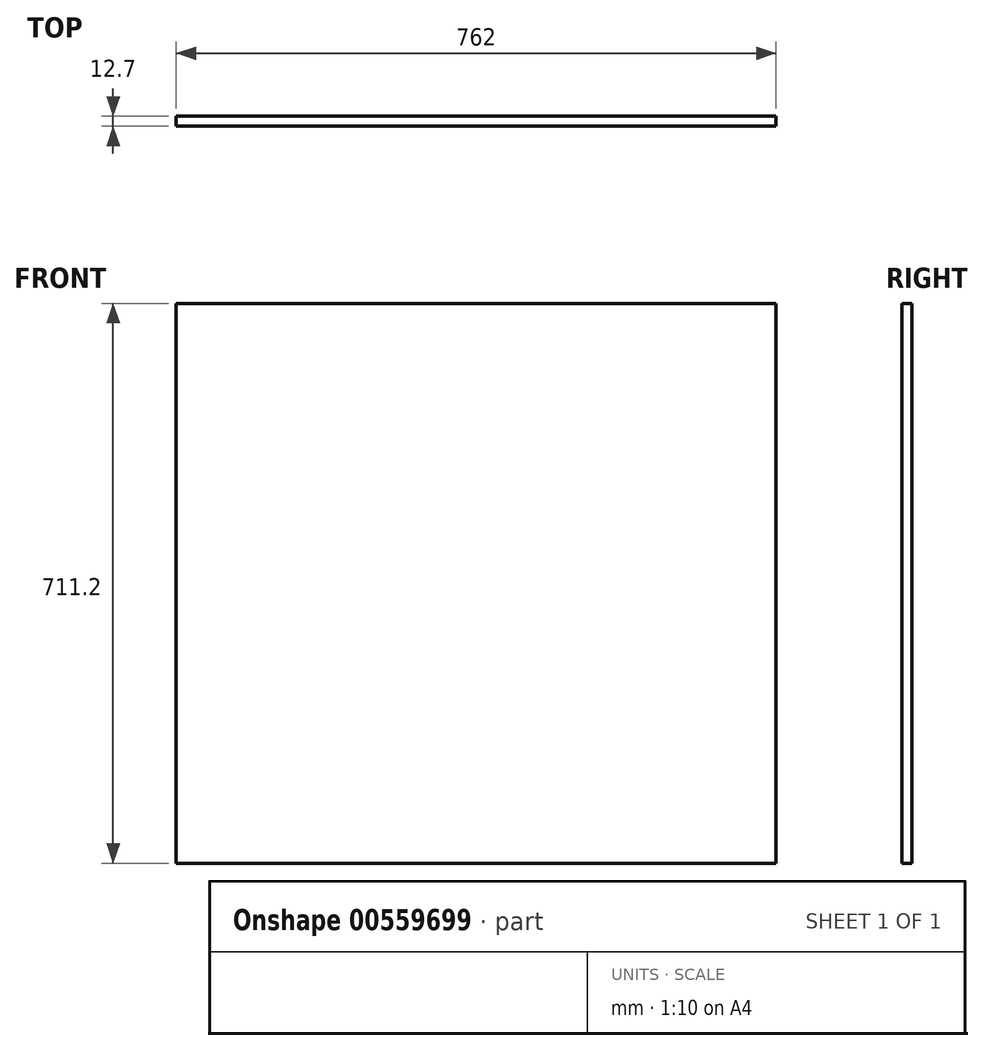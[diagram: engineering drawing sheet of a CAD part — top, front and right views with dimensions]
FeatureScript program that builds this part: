
annotation { "Feature Type Name" : "Feature", "Feature Type Description" : "" }
export const myFeature = defineFeature(function(context is Context, id is Id, definition is map)
    precondition{}
    {
        {
            var Q0;
            Q0=qCreatedBy(makeId("Front.planeOp"),FACE);
            var sketch = newSketch(context, id + "F0", { "sketchPlane" : qUnion([Q0])});
            skLineSegment(sketch, "E0.bottom", {"start": v(381, -355.6) * mm, "end": v(-381, -355.6) * mm});
            skLineSegment(sketch, "E0.top", {"start": v(381, 355.6) * mm, "end": v(-381, 355.6) * mm});
            skLineSegment(sketch, "E0.left", {"start": v(381, -355.6) * mm, "end": v(381, 355.6) * mm});
            skLineSegment(sketch, "E0.right", {"start": v(-381, -355.6) * mm, "end": v(-381, 355.6) * mm});
            skPoint(sketch, "E0.middle", {"position": v(0, 0) * mm});
            skSolve(sketch);
        }
        {
            var Q0;
            Q0 = qSketchRegion(id + "F0", true);
            extrude(context, id + "F1", {"entities" : qUnion([Q0]), "depth" : 12.7 * mm, "offsetDistance" : 25.4 * mm});
        }
    });
